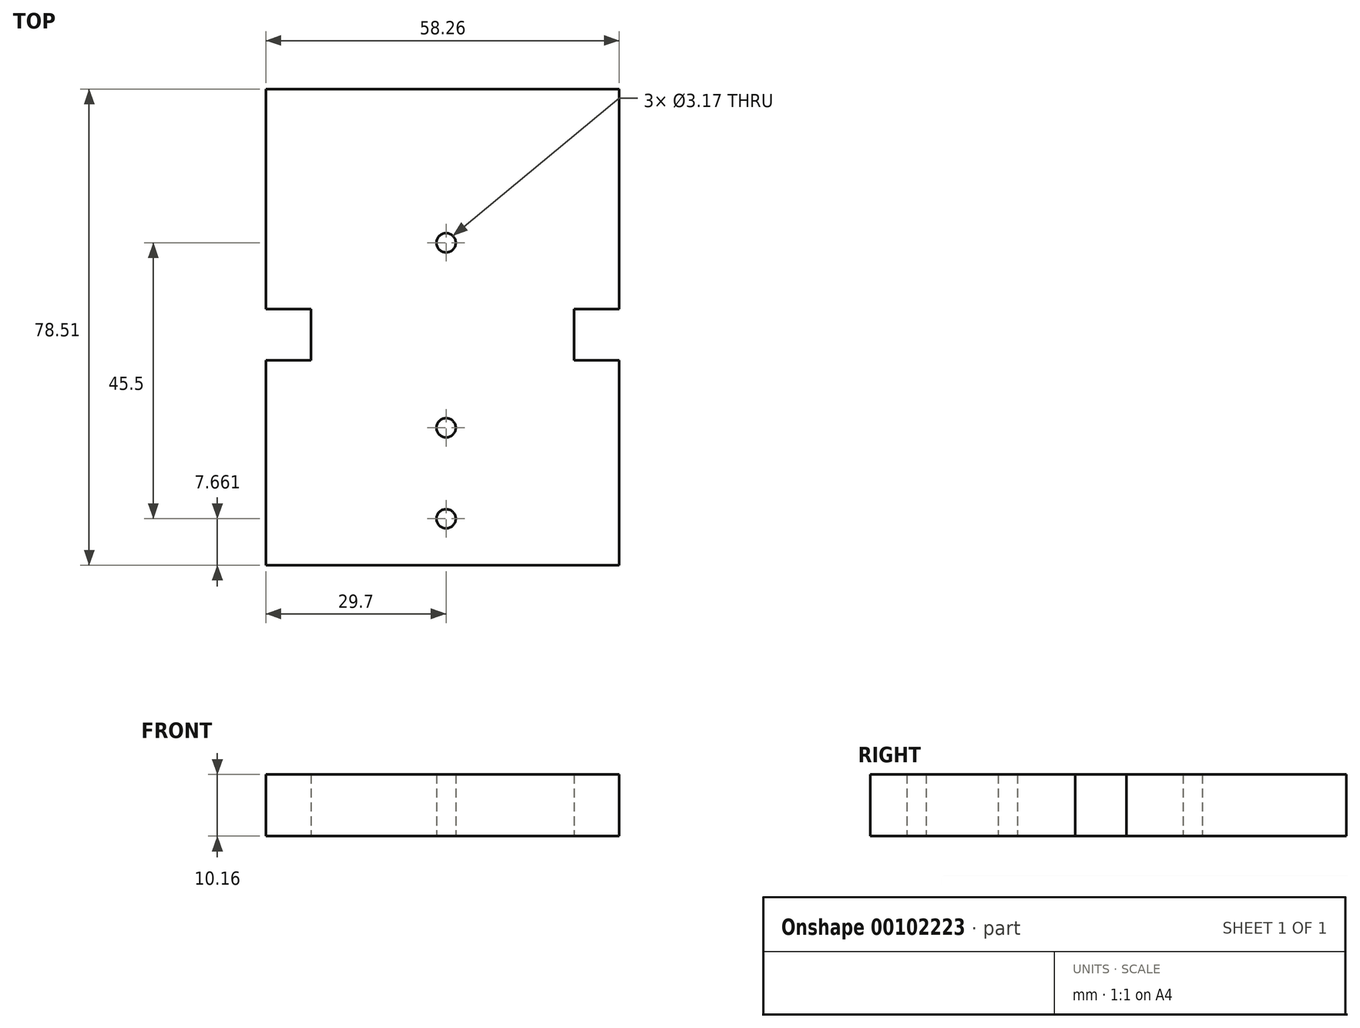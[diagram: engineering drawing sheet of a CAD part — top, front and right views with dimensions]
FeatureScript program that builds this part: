
annotation { "Feature Type Name" : "Feature", "Feature Type Description" : "" }
export const myFeature = defineFeature(function(context is Context, id is Id, definition is map)
    precondition{}
    {
        {
            var Q0;
            Q0=qCreatedBy(makeId("Top.planeOp"),FACE);
            var sketch = newSketch(context, id + "F0", { "sketchPlane" : qUnion([Q0])});
            skLineSegment(sketch, "E0.bottom", {"start": v(-29.7, 36.28) * mm, "end": v(28.56, 36.28) * mm});
            skLineSegment(sketch, "E0.top", {"start": v(-29.7, -42.23) * mm, "end": v(28.56, -42.23) * mm});
            skLineSegment(sketch, "E0.left", {"start": v(-29.7, 36.28) * mm, "end": v(-29.7, -42.23) * mm});
            skLineSegment(sketch, "E0.right", {"start": v(28.56, 36.28) * mm, "end": v(28.56, -42.23) * mm});
            skLineSegment(sketch, "E1.bottom", {"start": v(-29.7, 0) * mm, "end": v(-22.25, 0) * mm});
            skLineSegment(sketch, "E1.top", {"start": v(-29.7, -8.41) * mm, "end": v(-22.25, -8.41) * mm});
            skLineSegment(sketch, "E1.left", {"start": v(-29.7, 0) * mm, "end": v(-29.7, -8.41) * mm});
            skLineSegment(sketch, "E1.right", {"start": v(-22.25, 0) * mm, "end": v(-22.25, -8.41) * mm});
            skLineSegment(sketch, "E2.bottom", {"start": v(28.56, 0) * mm, "end": v(21.1, 0) * mm});
            skLineSegment(sketch, "E2.top", {"start": v(28.56, -8.41) * mm, "end": v(21.1, -8.41) * mm});
            skLineSegment(sketch, "E2.left", {"start": v(28.56, 0) * mm, "end": v(28.56, -8.41) * mm});
            skLineSegment(sketch, "E2.right", {"start": v(21.1, 0) * mm, "end": v(21.1, -8.41) * mm});
            skPoint(sketch, "E3", {"position": v(0, 10.93) * mm});
            skPoint(sketch, "E4", {"position": v(0, -19.57) * mm});
            skPoint(sketch, "E5", {"position": v(0, -34.57) * mm});
            skLineSegment(sketch, "E6", {"start": v(-23.04, 0.32) * mm, "end": v(-29.7, 0) * mm});
            skLineSegment(sketch, "E7", {"start": v(21.1, 0) * mm, "end": v(28.56, 0) * mm});
            skSolve(sketch);
        }
        {
            var Q0;
            {var subQ1=sQuery(id+"F0.wireOp",EDGE,"E0.bottom");Q0=makeQuery(id+"F0.imprint","IMPRINT",FACE,{"disambiguationData":[TD([[makeQuery(id+"F0.imprint","IMPRINT",EDGE,{"derivedFrom":subQ1}),-1.0]])]});}
            extrude(context, id + "F1", {"entities" : qUnion([Q0]), "depth" : 10.16 * mm});
        }
        {
            var Q0;
            Q0=sQuery(id+"F0.wireOp",VERTEX,"E3");
            var Q1;
            Q1=makeQuery(id+"F1.opExtrude","SWEPT_BODY",BODY,{"disambiguationData":[OSD([sQuery(id+"F0.wireOp",EDGE,"E0.bottom"),sQuery(id+"F0.wireOp",EDGE,"E0.top"),sQuery(id+"F0.wireOp",EDGE,"E0.left"),sQuery(id+"F0.wireOp",EDGE,"E0.right"),sQuery(id+"F0.wireOp",EDGE,"E1.bottom"),sQuery(id+"F0.wireOp",EDGE,"E1.top"),sQuery(id+"F0.wireOp",EDGE,"E1.right"),sQuery(id+"F0.wireOp",EDGE,"E2.bottom"),sQuery(id+"F0.wireOp",EDGE,"E2.top"),sQuery(id+"F0.wireOp",EDGE,"E2.right")])]});
            hole(context, id + "F2", {"style" : HoleStyle.SIMPLE, "endStyle" : HoleEndStyle.THROUGH, "oppositeDirection" : true, "holeDiameter" : 3.17 * mm, "locations" : qUnion([Q0]), "scope" : qUnion([Q1]), "isTappedThrough" : true});
        }
        {
            var Q0;
            Q0=sQuery(id+"F0.wireOp",VERTEX,"E4");
            var Q1;
            Q1=makeQuery(id+"F1.opExtrude","SWEPT_BODY",BODY,{"disambiguationData":[OSD([sQuery(id+"F0.wireOp",EDGE,"E0.bottom"),sQuery(id+"F0.wireOp",EDGE,"E0.top"),sQuery(id+"F0.wireOp",EDGE,"E0.left"),sQuery(id+"F0.wireOp",EDGE,"E0.right"),sQuery(id+"F0.wireOp",EDGE,"E1.bottom"),sQuery(id+"F0.wireOp",EDGE,"E1.top"),sQuery(id+"F0.wireOp",EDGE,"E1.right"),sQuery(id+"F0.wireOp",EDGE,"E2.bottom"),sQuery(id+"F0.wireOp",EDGE,"E2.top"),sQuery(id+"F0.wireOp",EDGE,"E2.right")])]});
            hole(context, id + "F3", {"style" : HoleStyle.SIMPLE, "endStyle" : HoleEndStyle.THROUGH, "oppositeDirection" : true, "holeDiameter" : 3.17 * mm, "locations" : qUnion([Q0]), "scope" : qUnion([Q1]), "isTappedThrough" : true});
        }
        {
            var Q0;
            Q0=sQuery(id+"F0.wireOp",VERTEX,"E5");
            var Q1;
            Q1=makeQuery(id+"F1.opExtrude","SWEPT_BODY",BODY,{"disambiguationData":[OSD([sQuery(id+"F0.wireOp",EDGE,"E0.bottom"),sQuery(id+"F0.wireOp",EDGE,"E0.top"),sQuery(id+"F0.wireOp",EDGE,"E0.left"),sQuery(id+"F0.wireOp",EDGE,"E0.right"),sQuery(id+"F0.wireOp",EDGE,"E1.bottom"),sQuery(id+"F0.wireOp",EDGE,"E1.top"),sQuery(id+"F0.wireOp",EDGE,"E1.right"),sQuery(id+"F0.wireOp",EDGE,"E2.bottom"),sQuery(id+"F0.wireOp",EDGE,"E2.top"),sQuery(id+"F0.wireOp",EDGE,"E2.right")])]});
            hole(context, id + "F4", {"style" : HoleStyle.SIMPLE, "endStyle" : HoleEndStyle.THROUGH, "oppositeDirection" : true, "holeDiameter" : 3.17 * mm, "locations" : qUnion([Q0]), "scope" : qUnion([Q1]), "isTappedThrough" : true});
        }
    });
